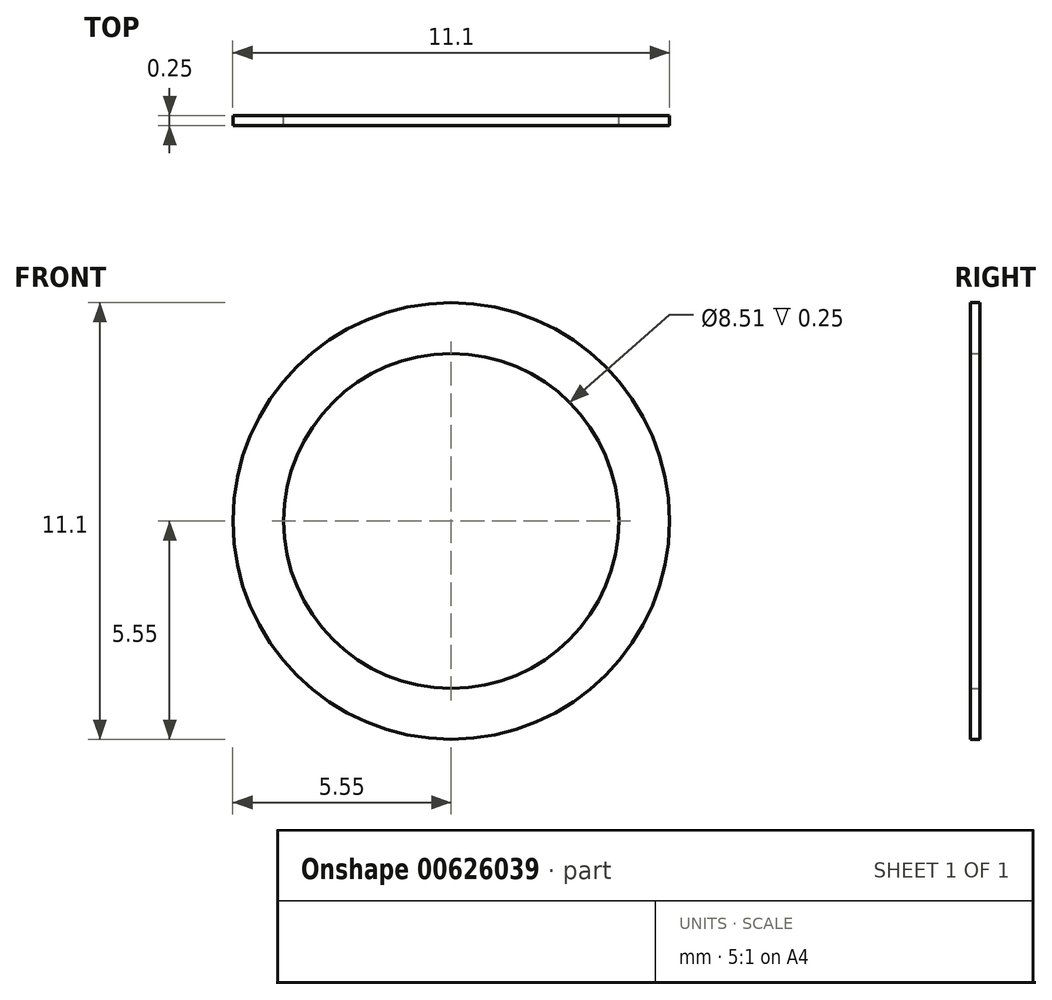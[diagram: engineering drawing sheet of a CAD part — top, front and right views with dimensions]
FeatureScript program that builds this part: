
annotation { "Feature Type Name" : "Feature", "Feature Type Description" : "" }
export const myFeature = defineFeature(function(context is Context, id is Id, definition is map)
    precondition{}
    {
        {
            var Q0;
            Q0=qCreatedBy(makeId("Front.planeOp"),FACE);
            var sketch = newSketch(context, id + "F0", { "sketchPlane" : qUnion([Q0])});
            skCircle(sketch, "E0", {"center": v(0, 0) * mm, "radius": 4.25 * mm});
            skCircle(sketch, "E1", {"center": v(0, 0) * mm, "radius": 5.55 * mm});
            skSolve(sketch);
        }
        {
            var Q0;
            Q0 = qSketchRegion(id + "F0", true);
            extrude(context, id + "F1", {"entities" : qUnion([Q0]), "depth" : 0.25 * mm, "offsetDistance" : 25 * mm});
        }
    });
